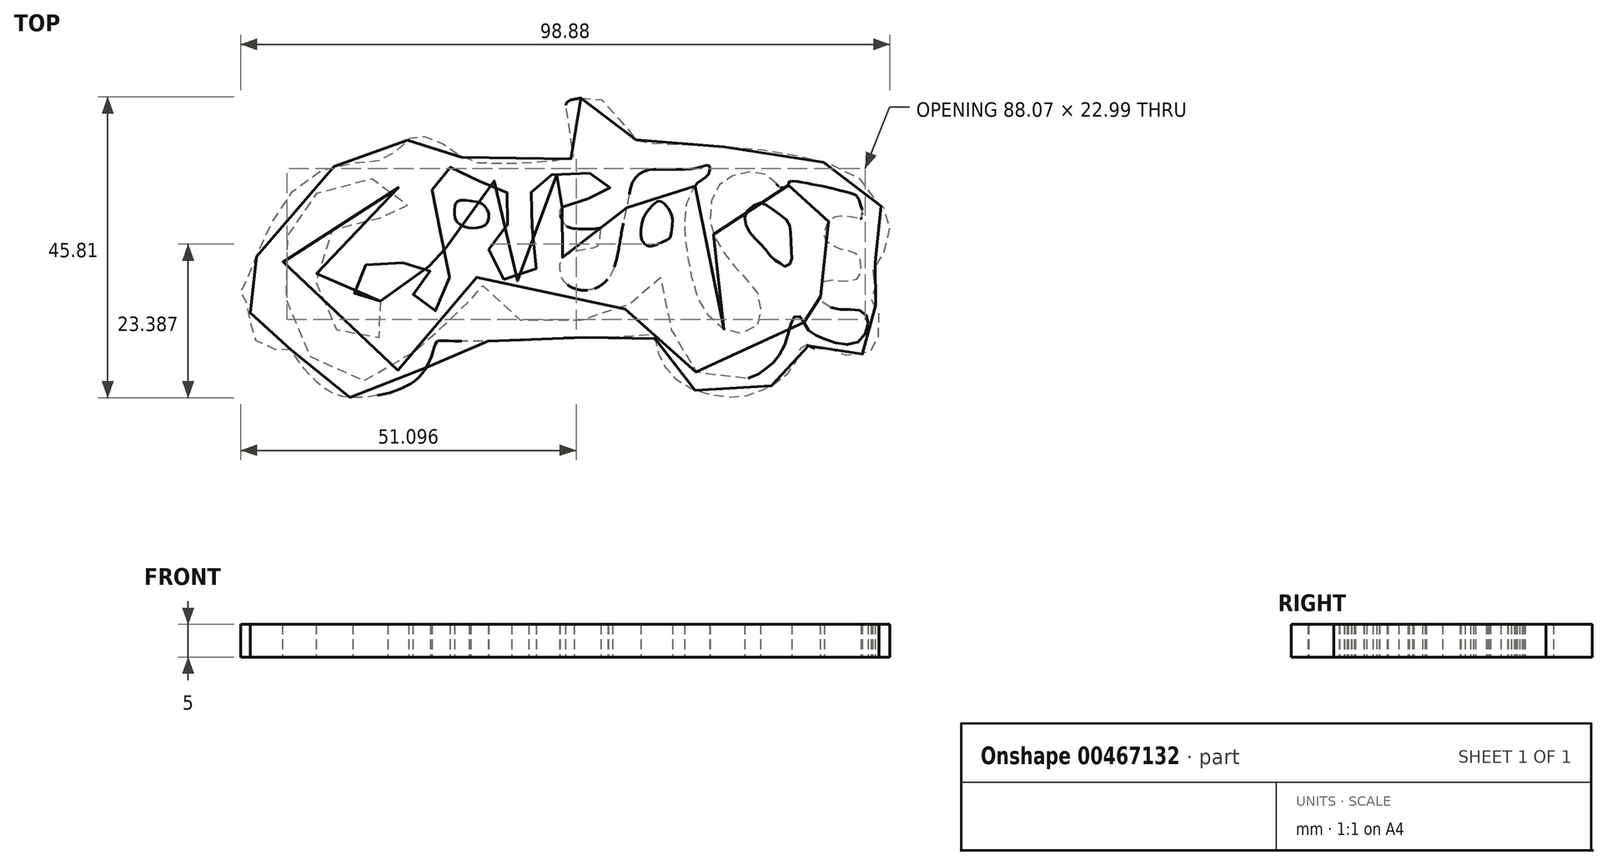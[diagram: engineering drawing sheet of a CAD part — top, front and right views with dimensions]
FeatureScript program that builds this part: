
annotation { "Feature Type Name" : "Feature", "Feature Type Description" : "" }
export const myFeature = defineFeature(function(context is Context, id is Id, definition is map)
    precondition{}
    {
        {
            var Q0;
            Q0=qCreatedBy(makeId("Top.planeOp"),FACE);
            var sketch = newSketch(context, id + "F0", { "sketchPlane" : qUnion([Q0])});
            skFitSpline(sketch, "E0", {"points": [v(-42.33, -15.72) * mm, v(-45.12, -15.66) * mm, v(-48.36, -13.18) * mm, v(-48.73, -9.31) * mm, v(-50, -7.38) * mm, v(-49.42, -5.67) * mm, v(-47, 0) * mm, v(-39.28, 10.85) * mm, v(-29.64, 13.01) * mm, v(-26.87, 14.11) * mm, v(-23.74, 16.77) * mm, v(-21.66, 16.61) * mm, v(-17.95, 14.92) * mm, v(-15, 12.96) * mm, v(-1.35, 13.17) * mm, v(0.74, 14.06) * mm, v(-0.53, 21.48) * mm, v(0.92, 22.46) * mm, v(4.31, 22.66) * mm, v(7.24, 19.9) * mm, v(10.68, 15.87) * mm, v(11.87, 15.73) * mm, v(21.55, 15.32) * mm, v(30.14, 14.65) * mm, v(39, 12.77) * mm, v(44.9, 9.68) * mm, v(47.07, 6.47) * mm, v(47.7, 6.05) * mm, v(48.39, 4.86) * mm, v(48.52, 0) * mm, v(46.4, -2.8) * mm, v(46.52, -5.22) * mm, v(46.5, -6.7) * mm, v(46, -7.9) * mm, v(46.77, -9.11) * mm, v(47.18, -11.93) * mm, v(46.64, -15.28) * mm, v(44.9, -16.35) * mm, v(40.88, -16.35) * mm, v(39.94, -15.7) * mm, v(37.93, -15.68) * mm, v(35.65, -14.9) * mm, v(34.97, -16.35) * mm, v(32.82, -19.85) * mm, v(29.74, -21.73) * mm, v(25.58, -22.99) * mm, v(19.13, -21.86) * mm, v(15.37, -19.3) * mm, v(13.5, -15.82) * mm, v(12.87, -13.65) * mm, v(10.95, -13.54) * mm, v(4.39, -13.87) * mm, v(0, -13.81) * mm, v(-5.98, -14.28) * mm, v(-19.21, -14.34) * mm, v(-20.18, -14.53) * mm, v(-21.38, -17.76) * mm, v(-24.9, -21.32) * mm, v(-31.82, -22.99) * mm, v(-37.25, -21.6) * mm, v(-41.91, -16.38) * mm, v(-42.33, -15.72) * mm]});
            skPoint(sketch, "E1.101.internal.snap0", {"position": v(50, 0) * mm});
            skFitSpline(sketch, "E1", {"points": [v(-28.78, -8.31) * mm, v(-28.04, -8.9) * mm, v(-27.63, -10.71) * mm, v(-27.83, -12.41) * mm, v(-29.24, -14.02) * mm, v(-31.1, -14.48) * mm, v(-32.26, -14.48) * mm, v(-34.33, -13.57) * mm, v(-36.4, -11.58) * mm, v(-37.6, -9.43) * mm, v(-38.47, -6.66) * mm, v(-38.38, -3.43) * mm, v(-37.76, -0.66) * mm, v(-36.48, 1.95) * mm, v(-34.5, 4.06) * mm, v(-32.47, 5.01) * mm, v(-29.57, 4.64) * mm, v(-27.34, 3.69) * mm, v(-25.18, 3.44) * mm, v(-24.65, 3.77) * mm, v(-24.6, 6.3) * mm, v(-26.76, 9.9) * mm, v(-27.67, 10.47) * mm, v(-29.07, 10.43) * mm, v(-32.1, 9.98) * mm, v(-36.32, 9.36) * mm, v(-38.05, 8.44) * mm, v(-40.29, 6.33) * mm, v(-41.12, 5.18) * mm, v(-42.48, 2.86) * mm, v(-43.35, -0.58) * mm, v(-43.64, -4.67) * mm, v(-42.98, -8.69) * mm, v(-41.57, -12.74) * mm, v(-40, -15.8) * mm, v(-38.67, -17.83) * mm, v(-35.24, -20.15) * mm, v(-31.23, -20.44) * mm, v(-27.42, -19.61) * mm, v(-24.52, -17.42) * mm, v(-22.9, -14.73) * mm, v(-22.45, -12.5) * mm, v(-21.87, -12) * mm, v(-19.6, -12) * mm, v(-17.07, -11.91) * mm, v(-15.5, -11.33) * mm, v(-15, -9.97) * mm, v(-15.13, -7.32) * mm, v(-15.17, -5.21) * mm, v(-14.67, -4.59) * mm, v(-13.89, -4.8) * mm, v(-13.18, -5.87) * mm, v(-11.12, -9.39) * mm, v(-10.41, -10.3) * mm, v(-7.93, -11.09) * mm, v(-4.87, -11.54) * mm, v(-0.9, -11.42) * mm, v(2.83, -11.09) * mm, v(6.26, -10.55) * mm, v(8.2, -9.76) * mm, v(9.28, -8.56) * mm, v(10.7, -5.83) * mm, v(11.68, -4.71) * mm, v(13.34, -4.42) * mm, v(14.62, -5.67) * mm, v(15.12, -8.4) * mm, v(15.37, -11.38) * mm, v(16.14, -15.3) * mm, v(17, -17.4) * mm, v(18.42, -18.62) * mm, v(20.63, -19.62) * mm, v(23.56, -20.26) * mm, v(25.91, -20.3) * mm, v(28.44, -19.62) * mm, v(30.33, -18.3) * mm, v(31.48, -17.23) * mm, v(32.76, -15.12) * mm, v(33.55, -12.62) * mm, v(34.12, -10.84) * mm, v(34.62, -10.6) * mm, v(35.33, -10.77) * mm, v(36, -12.13) * mm, v(37.26, -13.34) * mm, v(39, -14.1) * mm, v(41.7, -14.9) * mm, v(44.26, -14.36) * mm, v(45.47, -12.25) * mm, v(45.36, -10.63) * mm, v(44.15, -9.68) * mm, v(42.15, -9.6) * mm, v(40.07, -9.38) * mm, v(38.57, -8.36) * mm, v(38.26, -6.93) * mm, v(39, -5.22) * mm, v(41.06, -5.22) * mm, v(42.72, -5.22) * mm, v(44.04, -4.78) * mm, v(44.41, -3.76) * mm, v(44.41, -2.25) * mm, v(43.7, -1.08) * mm, v(42.04, -0.6) * mm, v(40.38, 0) * mm, v(39, 1.03) * mm, v(39, 2.43) * mm, v(39.66, 4.05) * mm, v(41.02, 4.69) * mm, v(43.17, 4.54) * mm, v(44.49, 4.27) * mm, v(44.6, 4.73) * mm, v(44.68, 5.22) * mm, v(44.15, 7.07) * mm, v(43.66, 7.82) * mm, v(42.41, 8.24) * mm, v(39.4, 9.03) * mm, v(36.87, 9.52) * mm, v(34.45, 9.93) * mm, v(33.47, 9.82) * mm, v(33.36, 9.25) * mm, v(32.64, 8.95) * mm, v(32.11, 8.95) * mm, v(31.66, 9.44) * mm, v(30.76, 10.54) * mm, v(29.17, 11.18) * mm, v(28.08, 11.4) * mm, v(25.7, 11) * mm, v(24.04, 10.39) * mm, v(22.83, 9.33) * mm, v(21.85, 7.48) * mm, v(21.4, 5.03) * mm, v(21.7, 2.65) * mm, v(22.57, 0.7) * mm, v(23.78, -1.23) * mm, v(24.64, -2.29) * mm, v(25.74, -3.65) * mm, v(27.25, -5.22) * mm, v(28.45, -6.63) * mm, v(29.1, -8.67) * mm, v(29.13, -10.74) * mm, v(28.72, -11.9) * mm, v(27.06, -13.15) * mm, v(24.68, -12.93) * mm, v(22.68, -12.1) * mm, v(21.02, -10.21) * mm, v(19.59, -7.8) * mm, v(18.83, -5.22) * mm, v(18.34, -2.63) * mm, v(17.9, -0.4) * mm, v(17.74, 1.78) * mm, v(17.63, 4.65) * mm, v(17.93, 6.65) * mm, v(18.76, 8.39) * mm, v(19.59, 9.7) * mm, v(20.83, 10.58) * mm, v(21.36, 11.44) * mm, v(21.32, 12.31) * mm, v(20.12, 12.16) * mm, v(18.57, 11.82) * mm, v(15.85, 11.78) * mm, v(13.63, 11.74) * mm, v(12.12, 11.67) * mm, v(10.65, 11.03) * mm, v(9.55, 9.56) * mm, v(9.03, 7.3) * mm, v(8.54, 4.92) * mm, v(8.12, 2.95) * mm, v(7.74, 0.7) * mm, v(7.37, -1.23) * mm, v(6.5, -4.02) * mm, v(4.99, -5.8) * mm, v(3.44, -6.51) * mm, v(1.56, -6.6) * mm, v(-0.44, -5.68) * mm, v(-1.31, -4.1) * mm, v(-1.21, -1.95) * mm, v(0, -1.03) * mm, v(1.82, -0.5) * mm, v(3.25, -0.24) * mm, v(3.96, -0.11) * mm, v(4.48, 0.27) * mm, v(4.7, 1) * mm, v(4.78, 2.61) * mm, v(4.78, 2.78) * mm, v(3.68, 2.67) * mm, v(2.7, 2.66) * mm, v(0.92, 2.72) * mm, v(-0.35, 3.1) * mm, v(-1.09, 4.07) * mm, v(-1.41, 5.19) * mm, v(-1.09, 6) * mm, v(-0.3, 6.65) * mm, v(0.5, 7.26) * mm, v(1.18, 7.3) * mm, v(3.7, 7.33) * mm, v(5.35, 7.51) * mm, v(5.93, 7.62) * mm, v(5.93, 8.3) * mm, v(6.43, 9.31) * mm, v(6.5, 10.64) * mm, v(5.5, 11.1) * mm, v(2.87, 11.15) * mm, v(0.57, 11.04) * mm, v(-1.38, 10.97) * mm, v(-3.03, 10.97) * mm, v(-4.4, 10.97) * mm, v(-5.04, 10.17) * mm, v(-5.7, 8.56) * mm, v(-6.05, 6.97) * mm, v(-6.12, 5.5) * mm, v(-5.76, 3.48) * mm, v(-5.33, 0.68) * mm, v(-5.08, -1.8) * mm, v(-5.12, -3.6) * mm, v(-6.38, -4.9) * mm, v(-7.92, -5.22) * mm, v(-10.51, -4.68) * mm, v(-11.74, -2.67) * mm, v(-12.2, -1.37) * mm, v(-12.2, -0.4) * mm, v(-11.09, 0.6) * mm, v(-10.08, 1.54) * mm, v(-9.54, 2.84) * mm, v(-8.93, 4.63) * mm, v(-8.79, 6.15) * mm, v(-9.1, 7.55) * mm, v(-9.8, 8.7) * mm, v(-11.16, 9.92) * mm, v(-12.53, 9.92) * mm, v(-14.04, 10.03) * mm, v(-15.48, 10.64) * mm, v(-16.45, 11.65) * mm, v(-17.89, 12.08) * mm, v(-19.61, 12.08) * mm, v(-20.37, 11.5) * mm, v(-20.84, 9.31) * mm, v(-20.8, 6.83) * mm, v(-20.4, 4.56) * mm, v(-19.25, 1.07) * mm, v(-18.5, -1.77) * mm, v(-18.2, -4.65) * mm, v(-18.25, -6.77) * mm, v(-18.9, -8.2) * mm, v(-20.58, -9.9) * mm, v(-21.99, -9.9) * mm, v(-23.03, -9.14) * mm, v(-23.79, -7.49) * mm, v(-23.17, -6.62) * mm, v(-21.95, -5.65) * mm, v(-21.23, -4.72) * mm, v(-21.23, -3.53) * mm, v(-21.8, -2.74) * mm, v(-23.5, -2.63) * mm, v(-24.86, -2.49) * mm, v(-27.13, -2.49) * mm, v(-29.25, -2.49) * mm, v(-30.7, -2.74) * mm, v(-32, -3.31) * mm, v(-32.83, -4.59) * mm, v(-32.87, -6.4) * mm, v(-32.21, -8) * mm, v(-30.9, -8.4) * mm, v(-29.59, -8.32) * mm, v(-28.78, -8.31) * mm]});
            skFitSpline(sketch, "E2", {"points": [v(-15.76, 7.03) * mm, v(-13.58, 6.66) * mm, v(-12.64, 5.88) * mm, v(-12.23, 4.48) * mm, v(-12.72, 3.34) * mm, v(-13.79, 2.88) * mm, v(-15.22, 2.84) * mm, v(-16.54, 3.34) * mm, v(-17.36, 4.2) * mm, v(-17.44, 5.55) * mm, v(-17.15, 6.78) * mm, v(-15.76, 7.03) * mm]});
            skFitSpline(sketch, "E3", {"points": [v(12.4, 0) * mm, v(14.6, 0.87) * mm, v(15.31, 1.28) * mm, v(15.73, 3.17) * mm, v(15.46, 5.23) * mm, v(14.1, 6.81) * mm, v(13.42, 6.85) * mm, v(12.09, 5.65) * mm, v(11.22, 4) * mm, v(10.9, 2.34) * mm, v(11.13, 0.89) * mm, v(11.78, 0.2) * mm, v(12.4, 0) * mm]});
            skFitSpline(sketch, "E4", {"points": [v(32.13, -2.56) * mm, v(32.96, -3.02) * mm, v(33.8, -2.4) * mm, v(33.86, -1.08) * mm, v(33.76, 1.86) * mm, v(33.53, 3.4) * mm, v(32.43, 4.65) * mm, v(30.24, 6.15) * mm, v(29.14, 6.69) * mm, v(27.38, 5.69) * mm, v(26.71, 4.33) * mm, v(27.4, 2.33) * mm, v(28.8, 0.73) * mm, v(30, -0.6) * mm, v(31.17, -1.95) * mm, v(32.13, -2.56) * mm]});
            skSolve(sketch);
        }
        {
            var Q0;
            Q0=makeQuery(id+"F0.imprint","IMPRINT",FACE,{"disambiguationData":[TD([[makeQuery(id+"F0.imprint","IMPRINT",EDGE,{"derivedFrom":sQuery(id+"F0.wireOp",EDGE,"E0")}),-1.0]])]});
            var Q1;
            Q1=makeQuery(id+"F0.imprint","IMPRINT",FACE,{"disambiguationData":[TD([[makeQuery(id+"F0.imprint","IMPRINT",EDGE,{"derivedFrom":sQuery(id+"F0.wireOp",EDGE,"E2")}),-1.0]])]});
            var Q2;
            Q2=makeQuery(id+"F0.imprint","IMPRINT",FACE,{"disambiguationData":[TD([[makeQuery(id+"F0.imprint","IMPRINT",EDGE,{"derivedFrom":sQuery(id+"F0.wireOp",EDGE,"E3")}),1.0]])]});
            var Q3;
            Q3=makeQuery(id+"F0.imprint","IMPRINT",FACE,{"disambiguationData":[TD([[makeQuery(id+"F0.imprint","IMPRINT",EDGE,{"derivedFrom":sQuery(id+"F0.wireOp",EDGE,"E4")}),1.0]])]});
            extrude(context, id + "F1", {"entities" : qUnion([Q0, Q1, Q2, Q3]), "depth" : 5 * mm});
        }
    });
